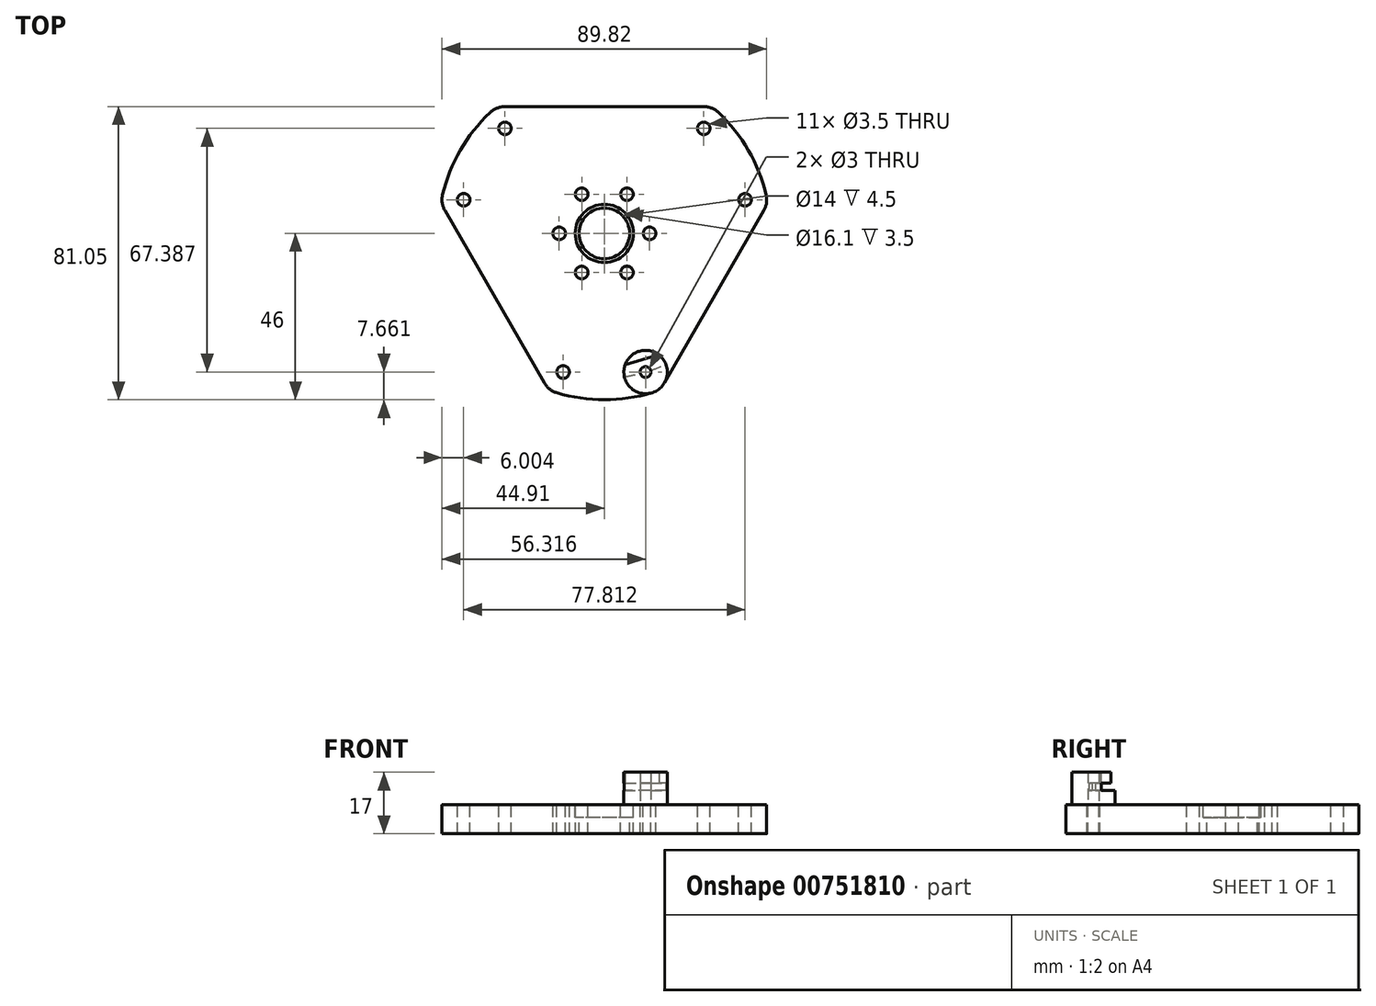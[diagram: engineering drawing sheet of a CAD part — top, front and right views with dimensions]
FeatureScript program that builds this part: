
annotation { "Feature Type Name" : "Feature", "Feature Type Description" : "" }
export const myFeature = defineFeature(function(context is Context, id is Id, definition is map)
    precondition{}
    {
        {
            var Q0;
            Q0=qCreatedBy(makeId("Top.planeOp"),FACE);
            var sketch = newSketch(context, id + "F0", { "sketchPlane" : qUnion([Q0])});
            skCircle(sketch, "E0", {"center": v(-38.9, 9.3) * mm, "radius": 1.75 * mm});
            skCircle(sketch, "E1", {"center": v(-38.9, 9.3) * mm, "radius": 6 * mm});
            skCircle(sketch, "E2", {"center": v(-11.4, -38.34) * mm, "radius": 1.75 * mm});
            skCircle(sketch, "E3", {"center": v(-11.4, -38.34) * mm, "radius": 6 * mm});
            skCircle(sketch, "E4", {"center": v(11.4, -38.34) * mm, "radius": 6 * mm});
            skCircle(sketch, "E5", {"center": v(11.4, -38.34) * mm, "radius": 1.5 * mm});
            skCircle(sketch, "E6", {"center": v(38.9, 9.3) * mm, "radius": 1.75 * mm});
            skCircle(sketch, "E7", {"center": v(38.9, 9.3) * mm, "radius": 6 * mm});
            skCircle(sketch, "E8", {"center": v(-27.5, 29.05) * mm, "radius": 1.75 * mm});
            skCircle(sketch, "E9", {"center": v(-27.5, 29.05) * mm, "radius": 6 * mm});
            skCircle(sketch, "E10", {"center": v(27.5, 29.05) * mm, "radius": 1.75 * mm});
            skCircle(sketch, "E11", {"center": v(27.5, 29.05) * mm, "radius": 6 * mm});
            skLineSegment(sketch, "E12", {"start": v(-27.5, 29.05) * mm, "end": v(27.5, 29.05) * mm});
            skLineSegment(sketch, "E13", {"start": v(38.9, 9.3) * mm, "end": v(11.4, -38.34) * mm, "construction": true});
            skLineSegment(sketch, "E14", {"start": v(-11.4, -38.34) * mm, "end": v(-38.9, 9.3) * mm});
            skCircle(sketch, "E15", {"center": v(0, 0) * mm, "radius": 40 * mm, "construction": true});
            skCircle(sketch, "E16", {"center": v(0, 0) * mm, "radius": 46 * mm});
            skLineSegment(sketch, "E17", {"start": v(-44.1, 6.3) * mm, "end": v(-16.6, -41.34) * mm});
            skLineSegment(sketch, "E18", {"start": v(16.6, -41.34) * mm, "end": v(44.1, 6.3) * mm});
            skLineSegment(sketch, "E19", {"start": v(27.5, 35.05) * mm, "end": v(-27.5, 35.05) * mm});
            skCircle(sketch, "E20", {"center": v(0, 0) * mm, "radius": 7 * mm});
            skCircle(sketch, "E21", {"center": v(0, 0) * mm, "radius": 8.05 * mm});
            skCircle(sketch, "E22.cCircle", {"center": v(0, 0) * mm, "radius": 12.5 * mm, "construction": true});
            skLineSegment(sketch, "E22.0", {"start": v(12.5, 0) * mm, "end": v(6.25, -10.83) * mm, "construction": true});
            skLineSegment(sketch, "E22.1", {"start": v(6.25, -10.83) * mm, "end": v(-6.25, -10.83) * mm, "construction": true});
            skLineSegment(sketch, "E22.2", {"start": v(-6.25, -10.83) * mm, "end": v(-12.5, 0) * mm, "construction": true});
            skLineSegment(sketch, "E22.3", {"start": v(-12.5, 0) * mm, "end": v(-6.25, 10.83) * mm, "construction": true});
            skLineSegment(sketch, "E22.4", {"start": v(-6.25, 10.83) * mm, "end": v(6.25, 10.83) * mm, "construction": true});
            skLineSegment(sketch, "E22.5", {"start": v(6.25, 10.83) * mm, "end": v(12.5, 0) * mm, "construction": true});
            skCircle(sketch, "E23", {"center": v(6.25, 10.83) * mm, "radius": 1.75 * mm});
            skCircle(sketch, "E24", {"center": v(12.5, 0) * mm, "radius": 1.75 * mm});
            skCircle(sketch, "E25", {"center": v(6.25, -10.83) * mm, "radius": 1.75 * mm});
            skCircle(sketch, "E26", {"center": v(-6.25, -10.83) * mm, "radius": 1.75 * mm});
            skCircle(sketch, "E27", {"center": v(-12.5, 0) * mm, "radius": 1.75 * mm});
            skCircle(sketch, "E28", {"center": v(-6.25, 10.83) * mm, "radius": 1.75 * mm});
            skCircle(sketch, "E29.cCircle", {"center": v(0, 0) * mm, "radius": 5 * mm, "construction": true});
            skLineSegment(sketch, "E29.0", {"start": v(5.58, 1.5) * mm, "end": v(4.08, -4.08) * mm, "construction": true});
            skLineSegment(sketch, "E29.1", {"start": v(4.08, -4.08) * mm, "end": v(-1.5, -5.58) * mm, "construction": true});
            skLineSegment(sketch, "E29.2", {"start": v(-1.5, -5.58) * mm, "end": v(-5.58, -1.5) * mm, "construction": true});
            skLineSegment(sketch, "E29.3", {"start": v(-5.58, -1.5) * mm, "end": v(-4.08, 4.08) * mm, "construction": true});
            skLineSegment(sketch, "E29.4", {"start": v(-4.08, 4.08) * mm, "end": v(1.5, 5.58) * mm, "construction": true});
            skLineSegment(sketch, "E29.5", {"start": v(1.5, 5.58) * mm, "end": v(5.58, 1.5) * mm, "construction": true});
            skPoint(sketch, "E29.0.midPoint", {"position": v(4.83, -1.3) * mm});
            skSolve(sketch);
        }
        {
            var Q0;
            {var subQ17=sQuery(id+"F0.wireOp",EDGE,"E18");Q0=makeQuery(id+"F0.imprint","IMPRINT",FACE,{"disambiguationData":[TD([[makeQuery(id+"F0.imprint","IMPRINT",EDGE,{"derivedFrom":subQ17}),1.0]])]});}
            var Q1;
            {var subQ0=sQuery(id+"F0.wireOp",EDGE,"E19");Q1=makeQuery(id+"F0.imprint","IMPRINT",FACE,{"disambiguationData":[TD([[makeQuery(id+"F0.imprint","IMPRINT",EDGE,{"derivedFrom":subQ0}),1.0]])]});}
            var Q2;
            Q2=makeQuery(id+"F0.imprint","IMPRINT",FACE,{"disambiguationData":[TD([[makeQuery(id+"F0.imprint","IMPRINT",EDGE,{"derivedFrom":sQuery(id+"F0.wireOp",EDGE,"E8")}),-1.0]])]});
            var Q3;
            Q3=makeQuery(id+"F0.imprint","IMPRINT",FACE,{"disambiguationData":[TD([[makeQuery(id+"F0.imprint","IMPRINT",EDGE,{"derivedFrom":sQuery(id+"F0.wireOp",EDGE,"E10")}),-1.0]])]});
            var Q4;
            Q4=makeQuery(id+"F0.imprint","IMPRINT",FACE,{"disambiguationData":[TD([[makeQuery(id+"F0.imprint","IMPRINT",EDGE,{"derivedFrom":sQuery(id+"F0.wireOp",EDGE,"E6")}),-1.0]])]});
            var Q5;
            Q5=makeQuery(id+"F0.imprint","IMPRINT",FACE,{"disambiguationData":[TD([[makeQuery(id+"F0.imprint","IMPRINT",EDGE,{"derivedFrom":sQuery(id+"F0.wireOp",EDGE,"E5")}),-1.0]])]});
            var Q6;
            Q6=makeQuery(id+"F0.imprint","IMPRINT",FACE,{"disambiguationData":[TD([[makeQuery(id+"F0.imprint","IMPRINT",EDGE,{"derivedFrom":sQuery(id+"F0.wireOp",EDGE,"E2")}),-1.0]])]});
            var Q7;
            {var subQ0=sQuery(id+"F0.wireOp",EDGE,"E17");Q7=makeQuery(id+"F0.imprint","IMPRINT",FACE,{"disambiguationData":[TD([[makeQuery(id+"F0.imprint","IMPRINT",EDGE,{"derivedFrom":subQ0}),1.0]])]});}
            var Q8;
            Q8=makeQuery(id+"F0.imprint","IMPRINT",FACE,{"disambiguationData":[TD([[makeQuery(id+"F0.imprint","IMPRINT",EDGE,{"derivedFrom":sQuery(id+"F0.wireOp",EDGE,"E0")}),-1.0]])]});
            var Q9;
            Q9=makeQuery(id+"F0.imprint","IMPRINT",FACE,{"disambiguationData":[TD([[makeQuery(id+"F0.imprint","IMPRINT",EDGE,{"derivedFrom":sQuery(id+"F0.wireOp",EDGE,"E20")}),-1.0]])]});
            extrude(context, id + "F1", {"entities" : qUnion([Q0, Q1, Q2, Q3, Q4, Q5, Q6, Q7, Q8, Q9]), "oppositeDirection" : true, "depth" : 8 * mm, "offsetDistance" : 25 * mm});
        }
        {
            var Q0;
            Q0=makeQuery(id+"F0.imprint","IMPRINT",FACE,{"disambiguationData":[TD([[makeQuery(id+"F0.imprint","IMPRINT",EDGE,{"derivedFrom":sQuery(id+"F0.wireOp",EDGE,"E20")}),-1.0]])]});
            extrude(context, id + "F2", {"entities" : qUnion([Q0]), "operationType" : NewBodyOperationType.REMOVE, "oppositeDirection" : true, "depth" : 3.5 * mm, "offsetDistance" : 25 * mm});
        }
        {
            var Q0;
            Q0=makeQuery(id+"F0.imprint","IMPRINT",FACE,{"disambiguationData":[TD([[makeQuery(id+"F0.imprint","IMPRINT",EDGE,{"derivedFrom":sQuery(id+"F0.wireOp",EDGE,"E5")}),-1.0]])]});
            extrude(context, id + "F3", {"entities" : qUnion([Q0]), "depth" : 4 * mm, "offsetDistance" : 25 * mm});
        }
        {
            var Q0;
            Q0=makeQuery(id+"F3.opExtrude","CAP_FACE",FACE,{"disambiguationData":[OSD([sQuery(id+"F0.wireOp",EDGE,"E4"),sQuery(id+"F0.wireOp",EDGE,"E5")])],"isStart":false});
            var sketch = newSketch(context, id + "F4", { "sketchPlane" : qUnion([Q0])});
            skCircle(sketch, "E30.0", {"center": v(0, 0) * mm, "radius": 40 * mm});
            skCircle(sketch, "E31.0", {"center": v(11.4, -38.34) * mm, "radius": 6 * mm});
            skCircle(sketch, "E32.0", {"center": v(11.4, -38.34) * mm, "radius": 1.5 * mm});
            skSolve(sketch);
        }
        {
            var Q0;
            {var subQ0=sQuery(id+"F4.wireOp",EDGE,"E31.0");var subQ1=sQuery(id+"F4.wireOp",EDGE,"E30.0");var subQ2=makeQuery(id+"F4.imprint","INTERSECT",VERTEX,{"disambiguationData":[OD(0.0)],"derivedFrom":[subQ1,subQ0]});Q0=makeQuery(id+"F4.imprint","IMPRINT",FACE,{"disambiguationData":[TD([[makeQuery(id+"F4.imprint","IMPRINT",EDGE,{"disambiguationData":[TD([[subQ2,-1.0]])],"derivedFrom":subQ1}),-1.0]])]});}
            var Q1;
            {var subQ0=sQuery(id+"F4.wireOp",EDGE,"E32.0");var subQ1=sQuery(id+"F4.wireOp",EDGE,"E30.0");var subQ2=makeQuery(id+"F4.imprint","INTERSECT",VERTEX,{"disambiguationData":[OD(0.0)],"derivedFrom":[subQ1,subQ0]});Q1=makeQuery(id+"F4.imprint","IMPRINT",FACE,{"disambiguationData":[TD([[makeQuery(id+"F4.imprint","IMPRINT",EDGE,{"disambiguationData":[TD([[subQ2,1.0]])],"derivedFrom":subQ1}),-1.0]])]});}
            extrude(context, id + "F5", {"entities" : qUnion([Q0, Q1]), "operationType" : NewBodyOperationType.ADD, "depth" : 2 * mm, "offsetDistance" : 25 * mm});
        }
        {
            var Q0;
            Q0=makeQuery(id+"F5.opExtrude","CAP_FACE",FACE,{"disambiguationData":[OSD([sQuery(id+"F4.wireOp",EDGE,"E30.0"),sQuery(id+"F4.wireOp",EDGE,"E31.0"),sQuery(id+"F4.wireOp",EDGE,"fa9509cc-951e-4ff0-b1e4-317579f6c50b.0")])],"isStart":false});
            var sketch = newSketch(context, id + "F6", { "sketchPlane" : qUnion([Q0])});
            skArc(sketch, "E33.0", {"start": v(17.01, -36.2) * mm, "mid": v(9.7, -32.59) * mm, "end": v(5.54, -39.61) * mm});
            skArc(sketch, "E34.0", {"start": v(5.54, -39.61) * mm, "mid": v(13.12, -44.1) * mm, "end": v(17.01, -36.2) * mm});
            skCircle(sketch, "E35.0", {"center": v(11.4, -38.34) * mm, "radius": 1.5 * mm});
            skLineSegment(sketch, "E36", {"start": v(0, 0) * mm, "end": v(11.4, -38.34) * mm, "construction": true});
            skPoint(sketch, "E37", {"position": v(10.4, -34.98) * mm});
            skLineSegment(sketch, "E38", {"start": v(5.74, -36.37) * mm, "end": v(15.08, -33.6) * mm});
            skSolve(sketch);
        }
        {
            var Q0;
            Q0=makeQuery(id+"F6.imprint","IMPRINT",FACE,{"disambiguationData":[TD([[makeQuery(id+"F6.imprint","IMPRINT",EDGE,{"derivedFrom":sQuery(id+"F6.wireOp",EDGE,"E34.0")}),1.0]])]});
            var Q1;
            {var subQ0=sQuery(id+"F6.wireOp",EDGE,"E33.0");Q1=makeQuery(id+"F6.imprint","IMPRINT",FACE,{"disambiguationData":[TD([[makeQuery(id+"F6.imprint","IMPRINT",EDGE,{"derivedFrom":subQ0}),1.0]])]});}
            var Q2;
            {var subQ0=sQuery(id+"F6.wireOp",EDGE,"edf9cec2-69db-4400-a145-b5983398bf3a.0");Q2=makeQuery(id+"F6.imprint","IMPRINT",FACE,{"disambiguationData":[TD([[makeQuery(id+"F6.imprint","IMPRINT",EDGE,{"derivedFrom":subQ0}),1.0]])]});}
            var Q3;
            {var subQ0=sQuery(id+"F6.wireOp",EDGE,"81c559a4-aee7-4d46-bca0-8c094127fd93.0");Q3=makeQuery(id+"F6.imprint","IMPRINT",FACE,{"disambiguationData":[TD([[makeQuery(id+"F6.imprint","IMPRINT",EDGE,{"derivedFrom":subQ0}),1.0]])]});}
            extrude(context, id + "F7", {"entities" : qUnion([Q0, Q1, Q2, Q3]), "operationType" : NewBodyOperationType.ADD, "depth" : 3 * mm, "offsetDistance" : 25 * mm});
        }
    });
